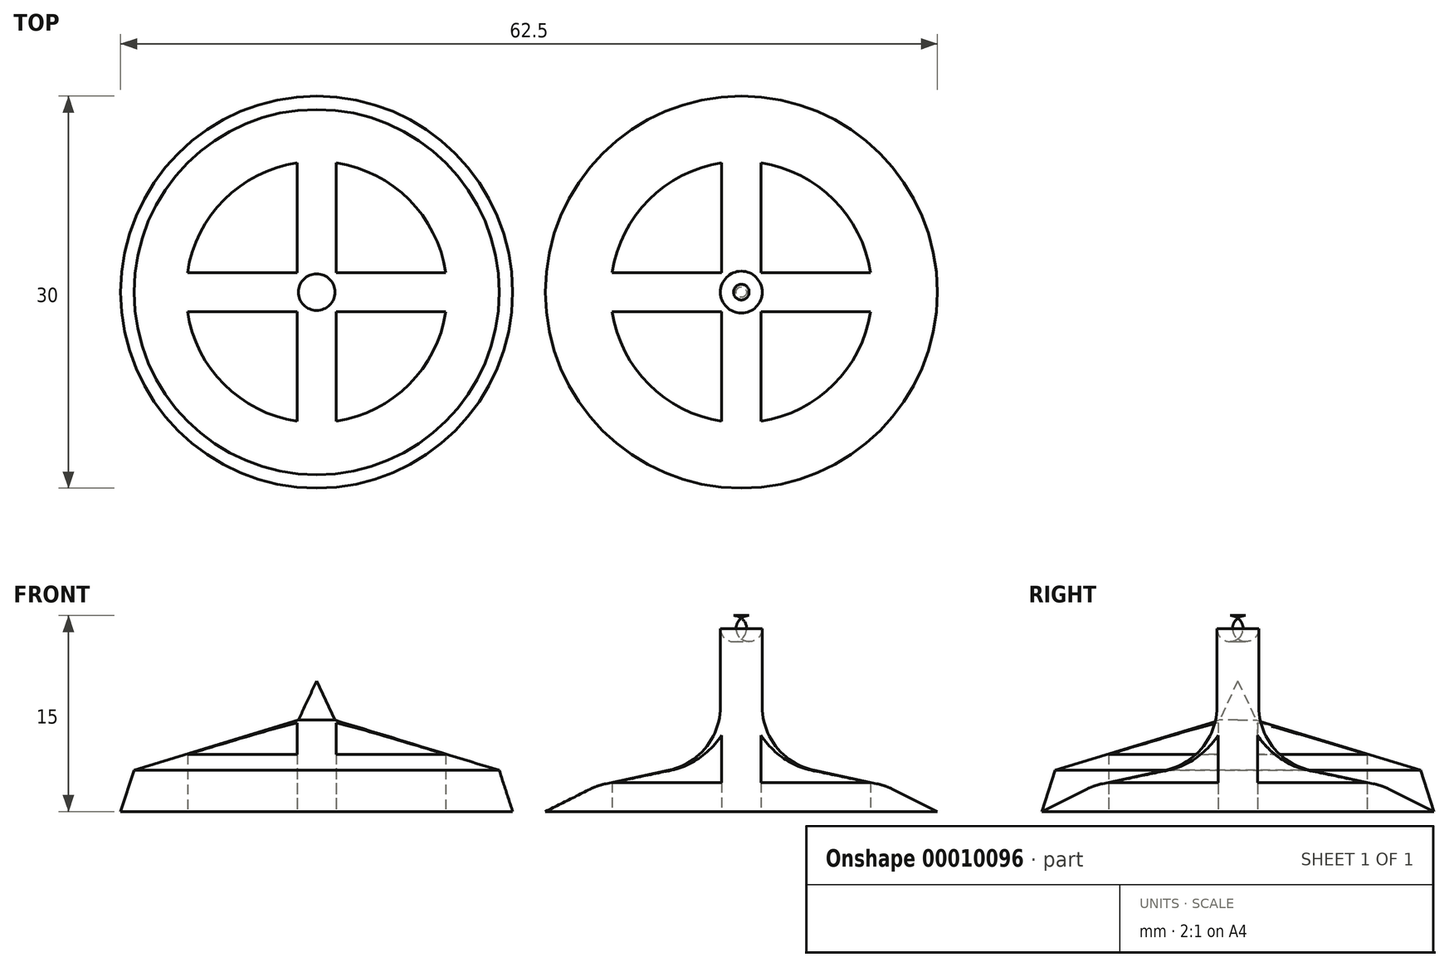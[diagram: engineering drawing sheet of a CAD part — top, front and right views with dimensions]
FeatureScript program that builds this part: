
annotation { "Feature Type Name" : "Feature", "Feature Type Description" : "" }
export const myFeature = defineFeature(function(context is Context, id is Id, definition is map)
    precondition{}
    {
        {
            var Q0;
            Q0=qCreatedBy(makeId("Front.planeOp"),FACE);
            var sketch = newSketch(context, id + "F0", { "sketchPlane" : qUnion([Q0])});
            skLineSegment(sketch, "E0", {"start": v(0, 0) * mm, "end": v(-15, 0) * mm});
            skLineSegment(sketch, "E1", {"start": v(-15, 0) * mm, "end": v(-13.98, 3.15) * mm});
            skLineSegment(sketch, "E2", {"start": v(-13.98, 3.15) * mm, "end": v(-1.4, 7) * mm});
            skLineSegment(sketch, "E3", {"start": v(-1.4, 7) * mm, "end": v(0, 10) * mm});
            skLineSegment(sketch, "E4", {"start": v(0, 10) * mm, "end": v(0, 0) * mm});
            skSolve(sketch);
        }
        {
            var Q0;
            Q0 = qSketchRegion(id + "F0", true);
            var Q1;
            Q1=sQuery(id+"F0.wireOp",EDGE,"E4");
            revolve(context, id + "F1", {"entities" : qUnion([Q0]), "axis" : qUnion([Q1]), "revolveType" : RevolveType.FULL});
        }
        {
            var Q0;
            Q0=makeQuery(id+"F1.opRevolve","SWEPT_FACE",FACE,{"disambiguationData":[OSD([sQuery(id+"F0.wireOp",EDGE,"E0")])]});
            var sketch = newSketch(context, id + "F2", { "sketchPlane" : qUnion([Q0])});
            skArc(sketch, "E5", {"start": v(-1.5, 9.89) * mm, "mid": v(-7.07, 7.07) * mm, "end": v(-9.89, 1.5) * mm});
            skLineSegment(sketch, "E6", {"start": v(-1.5, 9.89) * mm, "end": v(-1.5, 1.5) * mm});
            skLineSegment(sketch, "E7", {"start": v(1.5, 9.89) * mm, "end": v(1.5, 1.5) * mm});
            skLineSegment(sketch, "E8", {"start": v(9.89, 1.5) * mm, "end": v(1.5, 1.5) * mm});
            skLineSegment(sketch, "E9", {"start": v(-9.89, -1.5) * mm, "end": v(-1.5, -1.5) * mm});
            skLineSegment(sketch, "E10.trimOffspring", {"start": v(-1.5, -1.5) * mm, "end": v(-1.5, -9.89) * mm});
            skLineSegment(sketch, "E11.trimOffspring", {"start": v(1.5, -1.5) * mm, "end": v(1.5, -9.89) * mm});
            skLineSegment(sketch, "E12.trimOffspring", {"start": v(-1.5, 1.5) * mm, "end": v(-9.89, 1.5) * mm});
            skLineSegment(sketch, "E13.trimOffspring", {"start": v(1.5, -1.5) * mm, "end": v(9.89, -1.5) * mm});
            skArc(sketch, "E14.trimOffspring", {"start": v(-9.89, -1.5) * mm, "mid": v(-7.07, -7.07) * mm, "end": v(-1.5, -9.89) * mm});
            skArc(sketch, "E15.trimOffspring", {"start": v(9.89, 1.5) * mm, "mid": v(7.07, 7.07) * mm, "end": v(1.5, 9.89) * mm});
            skArc(sketch, "E16.trimOffspring", {"start": v(1.5, -9.89) * mm, "mid": v(7.07, -7.07) * mm, "end": v(9.89, -1.5) * mm});
            skSolve(sketch);
        }
        {
            var Q0;
            Q0 = qSketchRegion(id + "F2", true);
            extrude(context, id + "F3", {"entities" : qUnion([Q0]), "operationType" : NewBodyOperationType.REMOVE, "endBound" : BoundingType.UP_TO_NEXT, "oppositeDirection" : true, "depth" : 25 * mm});
        }
        {
            var Q0;
            Q0=qCreatedBy(makeId("Front.planeOp"),FACE);
            var sketch = newSketch(context, id + "F4", { "sketchPlane" : qUnion([Q0])});
            skLineSegment(sketch, "E17", {"start": v(17.5, 0) * mm, "end": v(32.5, 0) * mm});
            skLineSegment(sketch, "E18", {"start": v(32.5, 0) * mm, "end": v(32.5, 15) * mm});
            skLineSegment(sketch, "E19", {"start": v(32.5, 15) * mm, "end": v(30.9, 15) * mm});
            skLineSegment(sketch, "E20", {"start": v(30.9, 15) * mm, "end": v(30.9, 4) * mm});
            skLineSegment(sketch, "E21", {"start": v(30.9, 4) * mm, "end": v(21.5, 2) * mm});
            skLineSegment(sketch, "E22", {"start": v(21.5, 2) * mm, "end": v(17.5, 0) * mm});
            skSolve(sketch);
        }
        {
            var Q0;
            Q0=makeQuery(id+"F4.imprint","IMPRINT",FACE,{"disambiguationData":[TD([[makeQuery(id+"F4.imprint","IMPRINT",EDGE,{"derivedFrom":sQuery(id+"F4.wireOp",EDGE,"E17")}),1.0]])]});
            var Q1;
            Q1=sQuery(id+"F4.wireOp",EDGE,"E18");
            revolve(context, id + "F5", {"entities" : qUnion([Q0]), "axis" : qUnion([Q1]), "revolveType" : RevolveType.FULL});
        }
        {
            var Q0;
            Q0=makeQuery(id+"F5.opRevolve","SWEPT_FACE",FACE,{"disambiguationData":[OSD([sQuery(id+"F4.wireOp",EDGE,"E19")])]});
            fillet(context, id + "F6", {"entities" : qUnion([Q0]), "radius" : 1 * mm, "tangentPropagation" : true, "allowEdgeOverflow" : false});
        }
        {
            var Q0;
            Q0=makeQuery(id+"F5.opRevolve","SWEPT_EDGE",EDGE,{"disambiguationData":[OSD([sQuery(id+"F4.wireOp",EDGE,"E21"),sQuery(id+"F4.wireOp",EDGE,"E22")])]});
            fillet(context, id + "F7", {"entities" : qUnion([Q0]), "radius" : 5 * mm, "tangentPropagation" : true, "allowEdgeOverflow" : false});
        }
        {
            var Q0;
            Q0=makeQuery(id+"F5.opRevolve","SWEPT_EDGE",EDGE,{"disambiguationData":[OSD([sQuery(id+"F4.wireOp",EDGE,"E20"),sQuery(id+"F4.wireOp",EDGE,"E21")])]});
            fillet(context, id + "F8", {"entities" : qUnion([Q0]), "radius" : 5 * mm, "tangentPropagation" : true, "allowEdgeOverflow" : false});
        }
        {
            var Q0;
            Q0=makeQuery(id+"F5.opRevolve","SWEPT_FACE",FACE,{"disambiguationData":[OSD([sQuery(id+"F4.wireOp",EDGE,"E17")])]});
            var sketch = newSketch(context, id + "F9", { "sketchPlane" : qUnion([Q0])});
            skArc(sketch, "E23", {"start": v(22.61, -1.5) * mm, "mid": v(25.43, -7.07) * mm, "end": v(31, -9.89) * mm});
            skLineSegment(sketch, "E24", {"start": v(34, 9.89) * mm, "end": v(34, 1.5) * mm});
            skLineSegment(sketch, "E25", {"start": v(34, 1.5) * mm, "end": v(42.39, 1.5) * mm});
            skLineSegment(sketch, "E26", {"start": v(31, 9.89) * mm, "end": v(31, 1.5) * mm});
            skLineSegment(sketch, "E27", {"start": v(31, 1.5) * mm, "end": v(22.61, 1.5) * mm});
            skLineSegment(sketch, "E28", {"start": v(22.61, -1.5) * mm, "end": v(31, -1.5) * mm});
            skLineSegment(sketch, "E29", {"start": v(31, -1.5) * mm, "end": v(31, -9.89) * mm});
            skLineSegment(sketch, "E30", {"start": v(34, -9.89) * mm, "end": v(34, -1.5) * mm});
            skLineSegment(sketch, "E31", {"start": v(34, -1.5) * mm, "end": v(42.39, -1.5) * mm});
            skArc(sketch, "E32.trimOffspring", {"start": v(34, -9.89) * mm, "mid": v(39.57, -7.07) * mm, "end": v(42.39, -1.5) * mm});
            skArc(sketch, "E33.trimOffspring", {"start": v(42.39, 1.5) * mm, "mid": v(39.57, 7.07) * mm, "end": v(34, 9.89) * mm});
            skArc(sketch, "E34.trimOffspring", {"start": v(31, 9.89) * mm, "mid": v(25.43, 7.07) * mm, "end": v(22.61, 1.5) * mm});
            skSolve(sketch);
        }
        {
            var Q0;
            Q0 = qSketchRegion(id + "F9", true);
            extrude(context, id + "F10", {"entities" : qUnion([Q0]), "operationType" : NewBodyOperationType.REMOVE, "endBound" : BoundingType.UP_TO_NEXT, "oppositeDirection" : true, "depth" : 25 * mm});
        }
    });
